# Revit family: Sanitary_Shower-screens_Duscholux_DuschoGredel_DuschoSyna_Slider-twin-doors-bath
name_source: partatom
category: Plumbing Fixtures
revit_build: Autodesk Revit 2017 (Build: 20160225_1515(x64)
units: mm (PartAtom-declared; Revit-internal decimal feet)

## family parameters
Always vertical = Yes
Cut with Voids When Loaded = No
OmniClass Number = 23.45.00.00
OmniClass Title = Sanitary, Laundry, and Cleaning Equipment
Part Type = Normal
Room Calculation Point = No
Round Connector Dimension = Use Diameter
Shared = No
Work Plane-Based = No

## types (4) — shared parameters
Assembly Code = C1030200
Brand = Duscholux
Certified Quality UNE EN 14428 = http://www.duscholux.es
Combinations = Lateral 90°
Configuration enclosure = http://configuratumampara.duscholux.es
Description = 2 fixed segments + slider twin doors for bath
Design country = Spain / Germany
Edition number = 1
Environmental Management ISO 14001 = ECOEMBES Certificate
Fact Sheet = http://blob.duscholux.es
Glass Material = Glass_Material-Duscholux
Glass in Building UNE EN 12150 = CE Conformity marking
IFC Classification = Furnishing Element
Image = http://www.duscholux.es
Logo visibility = Yes
Maintenance and Cleaning = http://www.duscholux.es
Manufacturer = Duscholux Ibérica, S.A.
Manufacturer country = Spain
Manufacturer name = Duscholux Ibérica, S.A.
Max Height = 1600 mm  [stored 5.24934 ft]
Model = DuschoSyna
NBS Reference Code = 45-35-70
NBS Reference Description = Shower Enclosures
Net Weight (Kg) = 54
Opening System = Sliding
Opening System Image = http://blob.duscholux.es
Optional = Towel rail / Shelf
Product family = Duscho Gredel
Products = http://www.duscholux.es
Ref. = 6AW
Series = Duscho Gredel
Technical Inspection Certificate (Applus) = http://www.duscholux.es
Text visibility = Yes
Thickness Safety Glass Fixed Panels = 8 mm  [stored 0.0262467 ft]
Thickness Safety Glass Sliding = 5 mm  [stored 0.0164042 ft]
UNSPSC Code = 30181507
URL = http://www.duscholux.es
Uniclass 2015 Code = PR-40-20-06-79
Uniclass 2015 Description = Shower Enclosures
zero-valued in all types: Opening Door, Opening Percentage

## per-type parameters (varying)
| type | Accesories Material | Bath Height | Components | Handle Height | Handle Material | Height | Min Max Width | Product group | Sliding Door Width | Width |
| Platinum Aluminium Finish | Sillver Matt Finish | 450 mm  [stored 1.47638 ft] | European components | 1250 mm  [stored 4.10105 ft] | Chrome Finish | 1600 mm  [stored 5.24934 ft] | 1800 mm  [stored 5.90551 ft] | front for bath | 459 mm  [stored 1.50591 ft] | 1800 mm  [stored 5.90551 ft] |
| Silver Matt Aluminium Finish | Chrome Finish | 500 mm  [stored 1.64042 ft] | Eropean components | 1300 mm  [stored 4.26509 ft] | Chrome Finish | 1600 mm  [stored 5.24934 ft] | 1600 mm  [stored 5.24934 ft] | Front for bath | 409 mm  [stored 1.34186 ft] | 1600 mm  [stored 5.24934 ft] |
| White Aluminium Finish | White Finish | 450 mm  [stored 1.47638 ft] | Eropean components | 1250 mm  [stored 4.10105 ft] | White Finish | 1600 mm  [stored 5.24934 ft] | 1600 mm  [stored 5.24934 ft] | Front for bath | 409 mm  [stored 1.34186 ft] | 1600 mm  [stored 5.24934 ft] |
| Black Aluminium Finish | Chrome Finish | 573 mm | European components | 1373 mm | Chrome Finish | 1900 mm  [stored 6.2336 ft] | 2000 mm  [stored 6.56168 ft] | front for bath | 509 mm  [stored 1.66995 ft] | 2100 mm |

note: column(s) folded — value = type name in every type: Frame Material

note: [stored X ft] marks values corroborated as IEEE doubles in the binary element streams (Revit-internal decimal feet)

## geometry (parser evidence)
native form markers: Sweep x3
no freeform markers — native parametric forms only
